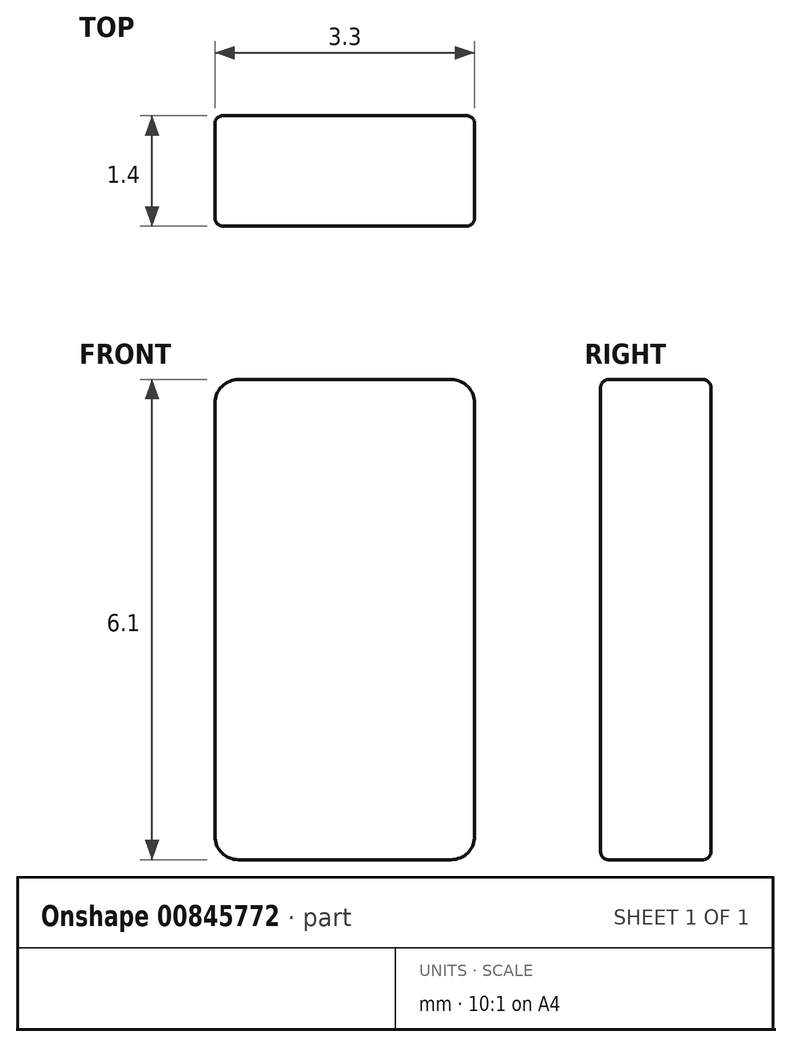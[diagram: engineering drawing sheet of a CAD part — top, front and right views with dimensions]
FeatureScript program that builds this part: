
annotation { "Feature Type Name" : "Feature", "Feature Type Description" : "" }
export const myFeature = defineFeature(function(context is Context, id is Id, definition is map)
    precondition{}
    {
        {
            var Q0;
            Q0=qCreatedBy(makeId("Front.planeOp"),FACE);
            var sketch = newSketch(context, id + "F0", { "sketchPlane" : qUnion([Q0])});
            skLineSegment(sketch, "E0.bottom", {"start": v(-1.65, 3.05) * mm, "end": v(1.65, 3.05) * mm});
            skLineSegment(sketch, "E0.top", {"start": v(-1.65, -3.05) * mm, "end": v(1.65, -3.05) * mm});
            skLineSegment(sketch, "E0.left", {"start": v(-1.65, 3.05) * mm, "end": v(-1.65, -3.05) * mm});
            skLineSegment(sketch, "E0.right", {"start": v(1.65, 3.05) * mm, "end": v(1.65, -3.05) * mm});
            skSolve(sketch);
        }
        {
            var Q0;
            Q0=makeQuery(id+"F0.imprint","IMPRINT",FACE,{"disambiguationData":[TD([[makeQuery(id+"F0.imprint","IMPRINT",EDGE,{"derivedFrom":sQuery(id+"F0.wireOp",EDGE,"E0.bottom")}),-1.0]])]});
            extrude(context, id + "F1", {"entities" : qUnion([Q0]), "depth" : 1.4 * mm, "offsetDistance" : 25 * mm});
        }
        {
            var Q0;
            Q0=makeQuery(id+"F1.opExtrude","SWEPT_EDGE",EDGE,{"disambiguationData":[OSD([sQuery(id+"F0.wireOp",EDGE,"E0.bottom"),sQuery(id+"F0.wireOp",EDGE,"E0.right")])]});
            var Q1;
            Q1=makeQuery(id+"F1.opExtrude","SWEPT_EDGE",EDGE,{"disambiguationData":[OSD([sQuery(id+"F0.wireOp",EDGE,"E0.bottom"),sQuery(id+"F0.wireOp",EDGE,"E0.left")])]});
            var Q2;
            Q2=makeQuery(id+"F1.opExtrude","SWEPT_EDGE",EDGE,{"disambiguationData":[OSD([sQuery(id+"F0.wireOp",EDGE,"E0.top"),sQuery(id+"F0.wireOp",EDGE,"E0.left")])]});
            var Q3;
            Q3=makeQuery(id+"F1.opExtrude","SWEPT_EDGE",EDGE,{"disambiguationData":[OSD([sQuery(id+"F0.wireOp",EDGE,"E0.top"),sQuery(id+"F0.wireOp",EDGE,"E0.right")])]});
            fillet(context, id + "F2", {"entities" : qUnion([Q0, Q1, Q2, Q3]), "radius" : .3 * mm, "tangentPropagation" : true, "allowEdgeOverflow" : false});
        }
        {
            var Q0;
            Q0=makeQuery(id+"F1.opExtrude","CAP_FACE",FACE,{"disambiguationData":[OSD([sQuery(id+"F0.wireOp",EDGE,"E0.bottom"),sQuery(id+"F0.wireOp",EDGE,"E0.top"),sQuery(id+"F0.wireOp",EDGE,"E0.left"),sQuery(id+"F0.wireOp",EDGE,"E0.right")])],"isStart":false});
            var Q1;
            Q1=makeQuery(id+"F1.opExtrude","CAP_FACE",FACE,{"disambiguationData":[OSD([sQuery(id+"F0.wireOp",EDGE,"E0.bottom"),sQuery(id+"F0.wireOp",EDGE,"E0.top"),sQuery(id+"F0.wireOp",EDGE,"E0.left"),sQuery(id+"F0.wireOp",EDGE,"E0.right")])],"isStart":true});
            fillet(context, id + "F3", {"entities" : qUnion([Q0, Q1]), "radius" : .1 * mm, "tangentPropagation" : true, "allowEdgeOverflow" : false});
        }
    });
